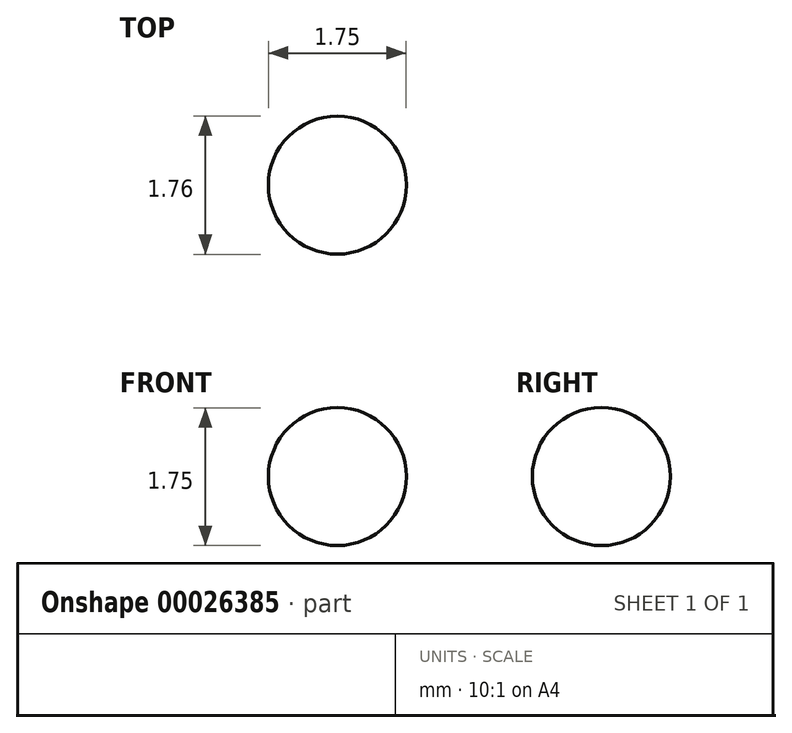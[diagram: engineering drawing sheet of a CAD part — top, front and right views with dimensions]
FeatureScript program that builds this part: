
annotation { "Feature Type Name" : "Feature", "Feature Type Description" : "" }
export const myFeature = defineFeature(function(context is Context, id is Id, definition is map)
    precondition{}
    {
        {
            var Q0;
            Q0=qCreatedBy(makeId("Front.planeOp"),FACE);
            var sketch = newSketch(context, id + "F0", { "sketchPlane" : qUnion([Q0])});
            skCircle(sketch, "E0", {"center": v(-12.51, 20.1) * mm, "radius": 0.88 * mm});
            skLineSegment(sketch, "E1", {"start": v(-12.51, 20.1) * mm, "end": v(-12.51, 20.97) * mm});
            skLineSegment(sketch, "E2", {"start": v(-12.51, 20.1) * mm, "end": v(-12.51, 19.22) * mm});
            skSolve(sketch);
        }
        {
            var Q0;
            {var subQ1=sQuery(id+"F0.wireOp",EDGE,"E1");Q0=makeQuery(id+"F0.imprint","IMPRINT",FACE,{"disambiguationData":[TD([[makeQuery(id+"F0.imprint","IMPRINT",EDGE,{"derivedFrom":subQ1}),1.0]])]});}
            var Q1;
            Q1=sQuery(id+"F0.wireOp",EDGE,"E2");
            revolve(context, id + "F1", {"entities" : qUnion([Q0]), "axis" : qUnion([Q1]), "revolveType" : RevolveType.FULL});
        }
    });
